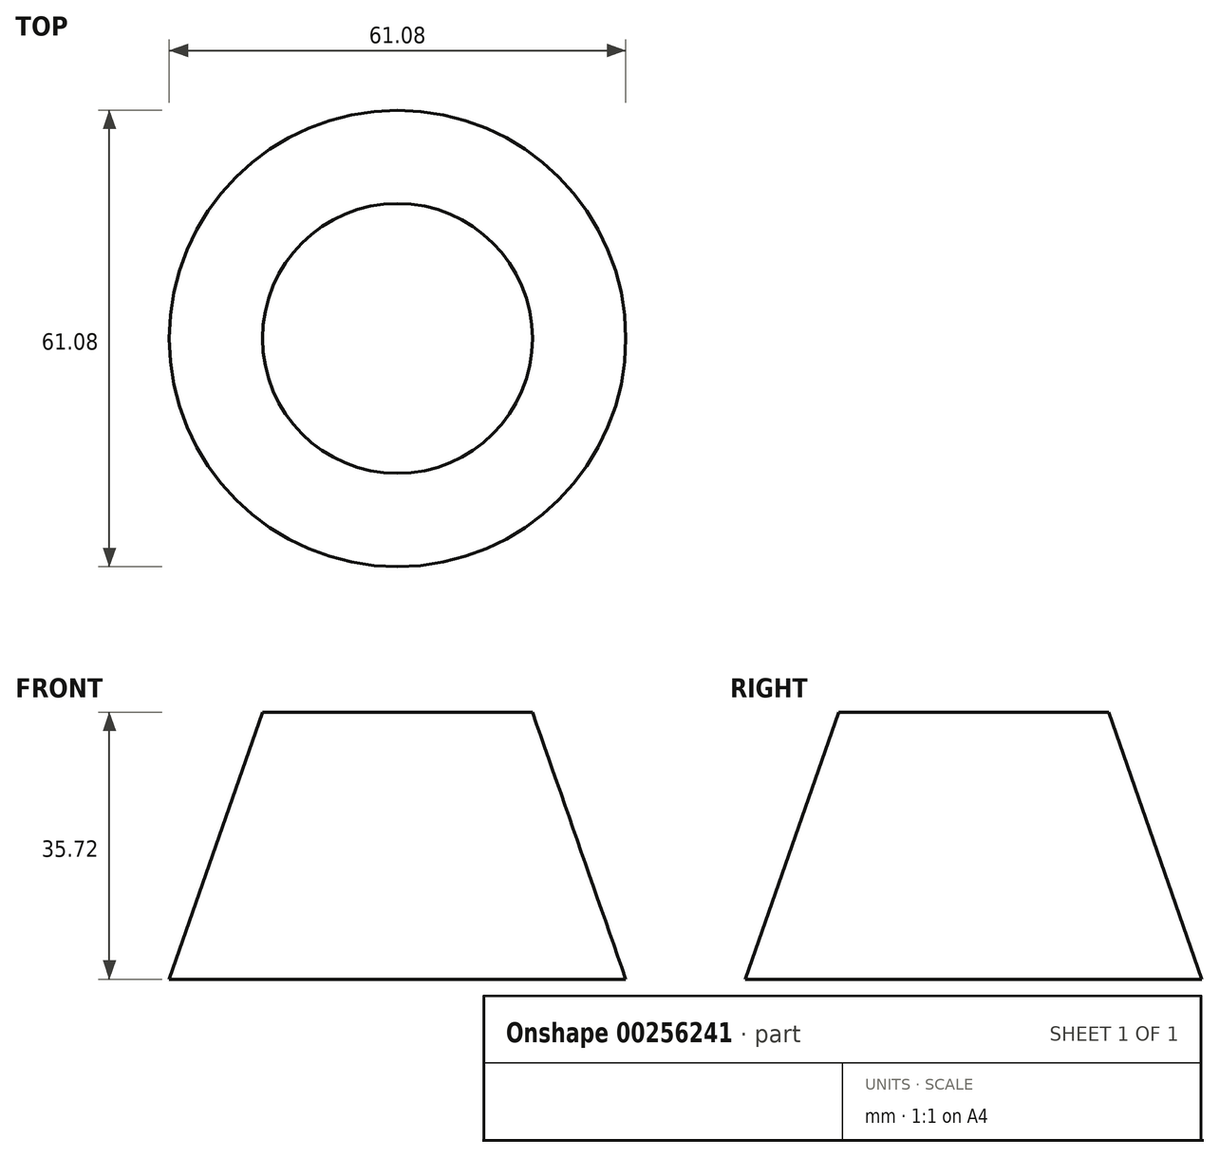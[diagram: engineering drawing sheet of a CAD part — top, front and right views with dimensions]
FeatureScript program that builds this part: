
annotation { "Feature Type Name" : "Feature", "Feature Type Description" : "" }
export const myFeature = defineFeature(function(context is Context, id is Id, definition is map)
    precondition{}
    {
        {
            var Q0;
            Q0=qCreatedBy(makeId("Front.planeOp"),FACE);
            var sketch = newSketch(context, id + "F0", { "sketchPlane" : qUnion([Q0])});
            skLineSegment(sketch, "E0", {"start": v(0, 0) * mm, "end": v(30.54, 0) * mm});
            skLineSegment(sketch, "E1", {"start": v(0, 0) * mm, "end": v(0, 35.72) * mm});
            skLineSegment(sketch, "E2", {"start": v(0, 35.72) * mm, "end": v(18.06, 35.72) * mm});
            skLineSegment(sketch, "E3", {"start": v(18.06, 35.72) * mm, "end": v(30.54, 0) * mm});
            skLineSegment(sketch, "E4", {"start": v(0, 55.11) * mm, "end": v(0, -22.7) * mm, "construction": true});
            skPoint(sketch, "E4.endSnap0", {"position": v(0, 17.86) * mm});
            skSolve(sketch);
        }
        {
            var Q0;
            Q0=makeQuery(id+"F0.imprint","IMPRINT",FACE,{"disambiguationData":[TD([[makeQuery(id+"F0.imprint","IMPRINT",EDGE,{"derivedFrom":sQuery(id+"F0.wireOp",EDGE,"E0")}),1.0]])]});
            var Q1;
            Q1=sQuery(id+"F0.wireOp",EDGE,"E4");
            revolve(context, id + "F1", {"entities" : qUnion([Q0]), "axis" : qUnion([Q1]), "revolveType" : RevolveType.FULL});
        }
    });
